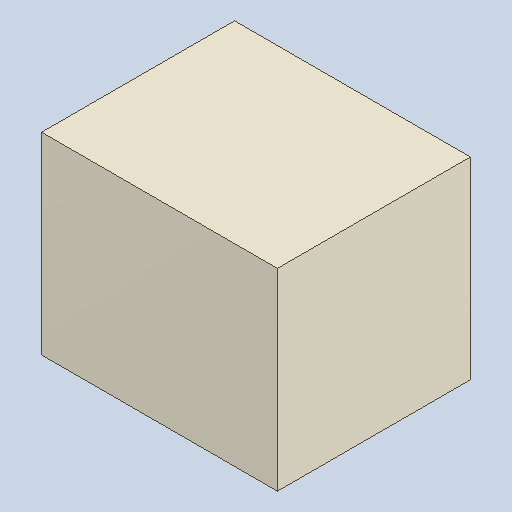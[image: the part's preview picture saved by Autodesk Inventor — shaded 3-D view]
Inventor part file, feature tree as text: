
AUTODESK INVENTOR PART (.ipt)
format: ipt  version: 2023.4 (Build 274418000, 418)  size: 81,920 bytes
history: native  units: mm
features: extrude x1
ambient origin geometry x8: Origin, YZ Plane, XZ Plane, XY Plane, X Axis, Y Axis, Z Axis, Center Point
bodies: Solid1 (feature_tree)
feature tree (1):
  extrude  "Extruded_18"  [1 undecoded]
note: 1 required parameter value undecoded (feature->parameter linkage not recoverable at this tier; creation-order binding heuristic only, values carry confidence <= 0.55)
